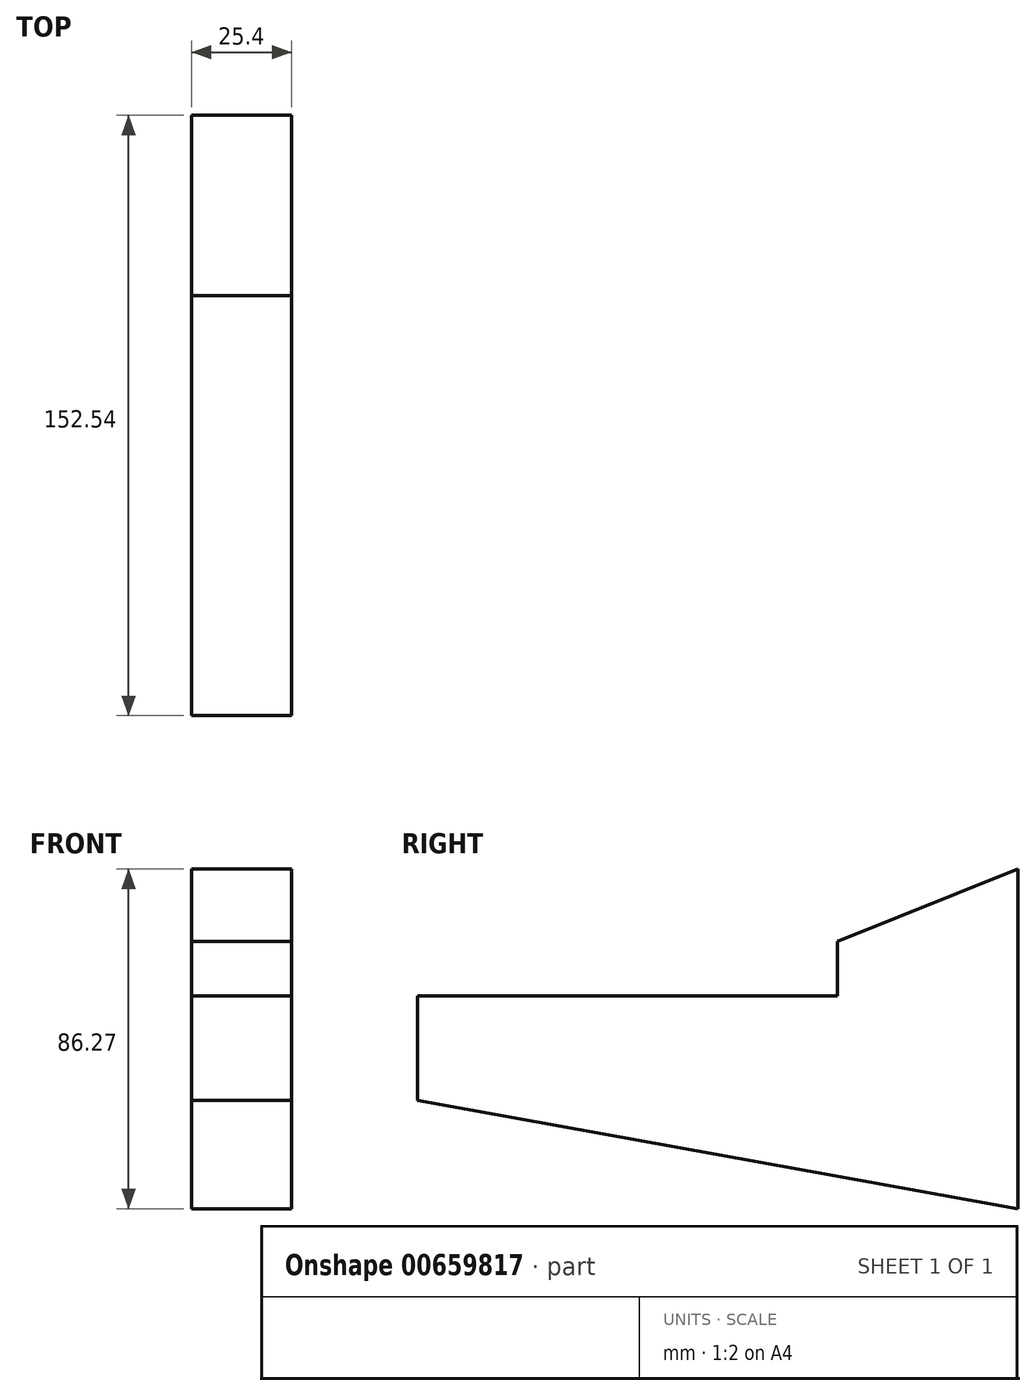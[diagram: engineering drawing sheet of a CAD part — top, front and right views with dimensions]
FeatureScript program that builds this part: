
annotation { "Feature Type Name" : "Feature", "Feature Type Description" : "" }
export const myFeature = defineFeature(function(context is Context, id is Id, definition is map)
    precondition{}
    {
        {
            var Q0;
            Q0=qCreatedBy(makeId("Right.planeOp"),FACE);
            var sketch = newSketch(context, id + "F0", { "sketchPlane" : qUnion([Q0])});
            skLineSegment(sketch, "E0", {"start": v(-75.67, 0) * mm, "end": v(75.6, 0) * mm});
            skLineSegment(sketch, "E1", {"start": v(75.6, 0) * mm, "end": v(-75.67, 0) * mm});
            skLineSegment(sketch, "E2", {"start": v(-75.67, 0) * mm, "end": v(-75.67, -26.52) * mm});
            skLineSegment(sketch, "E3", {"start": v(76.87, -26.52) * mm, "end": v(76.87, -54.01) * mm});
            skLineSegment(sketch, "E4", {"start": v(76.87, -54.01) * mm, "end": v(-75.67, -26.52) * mm});
            skLineSegment(sketch, "E5", {"start": v(76.87, 32.26) * mm, "end": v(76.87, -26.52) * mm});
            skLineSegment(sketch, "E6", {"start": v(76.87, -26.52) * mm, "end": v(31.04, 0) * mm});
            skLineSegment(sketch, "E7", {"start": v(31.04, 0) * mm, "end": v(31.04, 13.93) * mm});
            skLineSegment(sketch, "E8", {"start": v(31.04, 13.93) * mm, "end": v(76.87, 32.26) * mm});
            skLineSegment(sketch, "E9", {"start": v(0, 29.82) * mm, "end": v(29.33, -22.73) * mm});
            skLineSegment(sketch, "E10", {"start": v(29.33, -22.73) * mm, "end": v(21.5, 28.17) * mm});
            skSolve(sketch);
        }
        {
            var Q0;
            Q0 = qSketchRegion(id + "F0", true);
            extrude(context, id + "F1", {"entities" : qUnion([Q0]), "depth" : 25.4 * mm, "offsetDistance" : 25.4 * mm});
        }
    });
